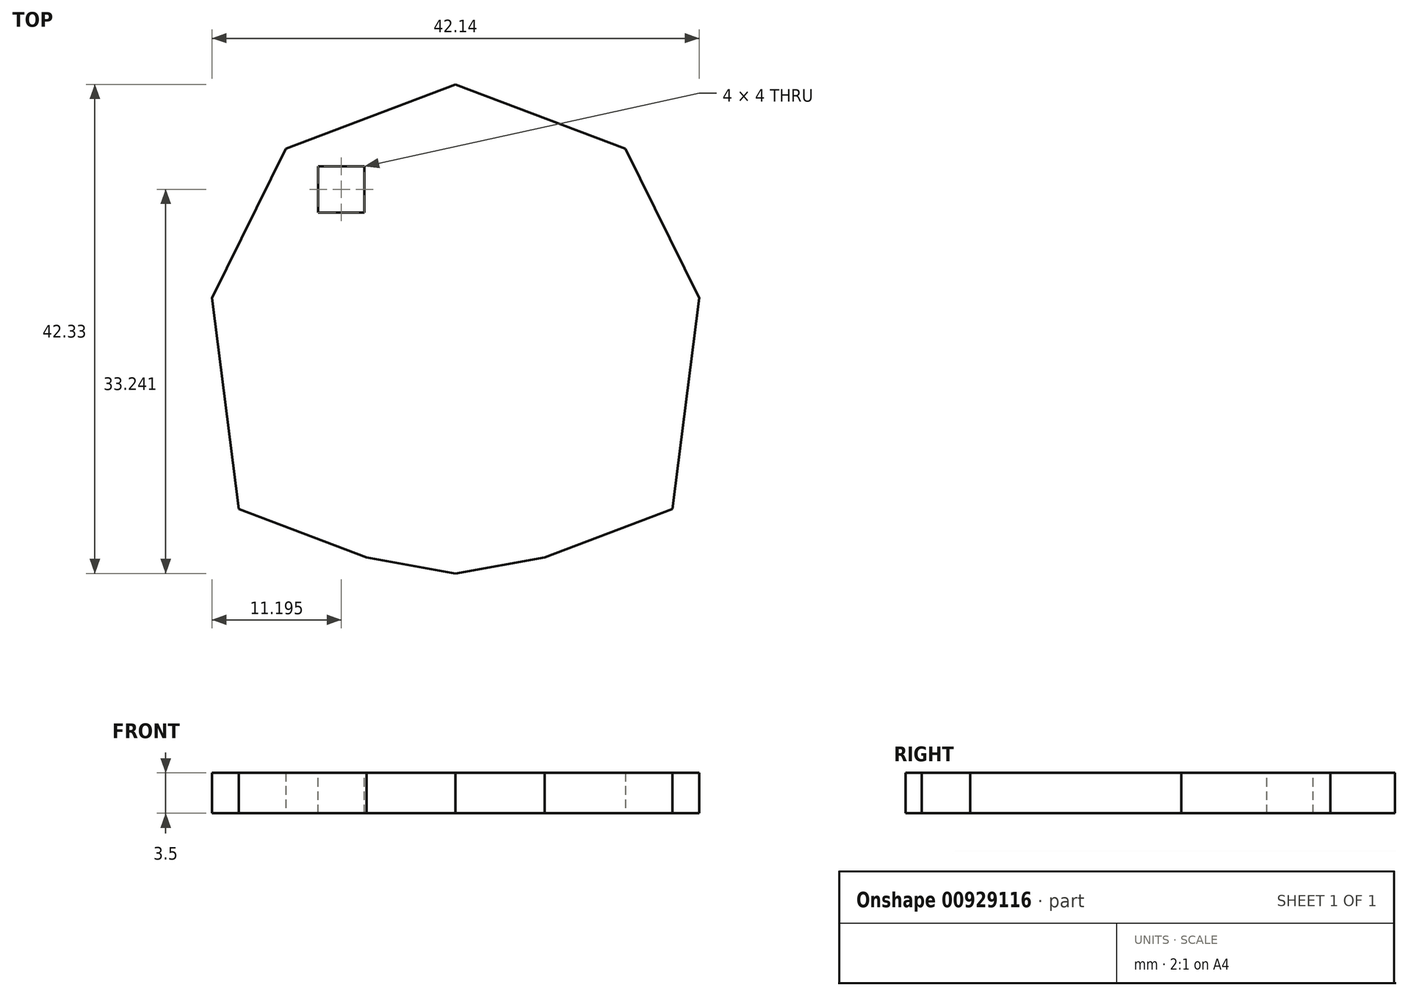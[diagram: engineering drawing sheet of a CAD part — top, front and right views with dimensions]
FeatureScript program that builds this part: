
annotation { "Feature Type Name" : "Feature", "Feature Type Description" : "" }
export const myFeature = defineFeature(function(context is Context, id is Id, definition is map)
    precondition{}
    {
        {
            var Q0;
            Q0=qCreatedBy(makeId("Top.planeOp"),FACE);
            var sketch = newSketch(context, id + "F0", { "sketchPlane" : qUnion([Q0])});
            skLineSegment(sketch, "E0", {"start": v(-18.75, 0) * mm, "end": v(18.75, 0) * mm, "construction": true});
            skLineSegment(sketch, "E1", {"start": v(0, 0) * mm, "end": v(0, 38.2) * mm});
            skSolve(sketch);
        }
        {
            var Q0;
            Q0=qCreatedBy(makeId("Top.planeOp"),FACE);
            var sketch = newSketch(context, id + "F1", { "sketchPlane" : qUnion([Q0])});
            skLineSegment(sketch, "E2", {"start": v(-18.75, 0) * mm, "end": v(-21.07, 18.25) * mm});
            skLineSegment(sketch, "E3", {"start": v(-21.07, 18.25) * mm, "end": v(-14.68, 31.16) * mm});
            skLineSegment(sketch, "E4", {"start": v(-14.68, 31.16) * mm, "end": v(0, 36.74) * mm});
            skLineSegment(sketch, "E5", {"start": v(-18.75, 0) * mm, "end": v(-7.7, -4.2) * mm});
            skLineSegment(sketch, "E6", {"start": v(0, -5.6) * mm, "end": v(-7.7, -4.2) * mm});
            skLineSegment(sketch, "E7.MirrorCS", {"start": v(14.68, 31.16) * mm, "end": v(0, 36.74) * mm});
            skLineSegment(sketch, "E8.MirrorCS", {"start": v(21.07, 18.25) * mm, "end": v(14.68, 31.16) * mm});
            skLineSegment(sketch, "E9.MirrorCS", {"start": v(18.75, 0) * mm, "end": v(21.07, 18.25) * mm});
            skLineSegment(sketch, "E10.MirrorCS", {"start": v(18.75, 0) * mm, "end": v(7.7, -4.2) * mm});
            skLineSegment(sketch, "E11.MirrorCS", {"start": v(0, -5.6) * mm, "end": v(7.7, -4.2) * mm});
            skSolve(sketch);
        }
        {
            var Q0;
            Q0 = qSketchRegion(id + "F1", true);
            extrude(context, id + "F2", {"entities" : qUnion([Q0]), "depth" : 3.5 * mm, "offsetDistance" : 25 * mm});
        }
        {
            var Q0;
            Q0=makeQuery(id+"F2.opExtrude","CAP_FACE",FACE,{"disambiguationData":[OSD([sQuery(id+"F1.wireOp",EDGE,"E2"),sQuery(id+"F1.wireOp",EDGE,"E3"),sQuery(id+"F1.wireOp",EDGE,"E4"),sQuery(id+"F1.wireOp",EDGE,"E5"),sQuery(id+"F1.wireOp",EDGE,"E6"),sQuery(id+"F1.wireOp",EDGE,"E7.MirrorCS"),sQuery(id+"F1.wireOp",EDGE,"E8.MirrorCS"),sQuery(id+"F1.wireOp",EDGE,"E9.MirrorCS"),sQuery(id+"F1.wireOp",EDGE,"E10.MirrorCS"),sQuery(id+"F1.wireOp",EDGE,"E11.MirrorCS")])],"isStart":false});
            var sketch = newSketch(context, id + "F3", { "sketchPlane" : qUnion([Q0])});
            skLineSegment(sketch, "E12.bottom", {"start": v(-11.88, 25.65) * mm, "end": v(-7.88, 25.65) * mm});
            skLineSegment(sketch, "E12.top", {"start": v(-11.88, 29.65) * mm, "end": v(-7.88, 29.65) * mm});
            skLineSegment(sketch, "E12.left", {"start": v(-11.88, 25.65) * mm, "end": v(-11.88, 29.65) * mm});
            skLineSegment(sketch, "E12.right", {"start": v(-7.88, 25.65) * mm, "end": v(-7.88, 29.65) * mm});
            skSolve(sketch);
        }
        {
            var Q0;
            Q0 = qSketchRegion(id + "F3", true);
            extrude(context, id + "F4", {"entities" : qUnion([Q0]), "operationType" : NewBodyOperationType.REMOVE, "endBound" : BoundingType.THROUGH_ALL, "oppositeDirection" : true, "depth" : 25 * mm, "offsetDistance" : 25 * mm});
        }
    });
